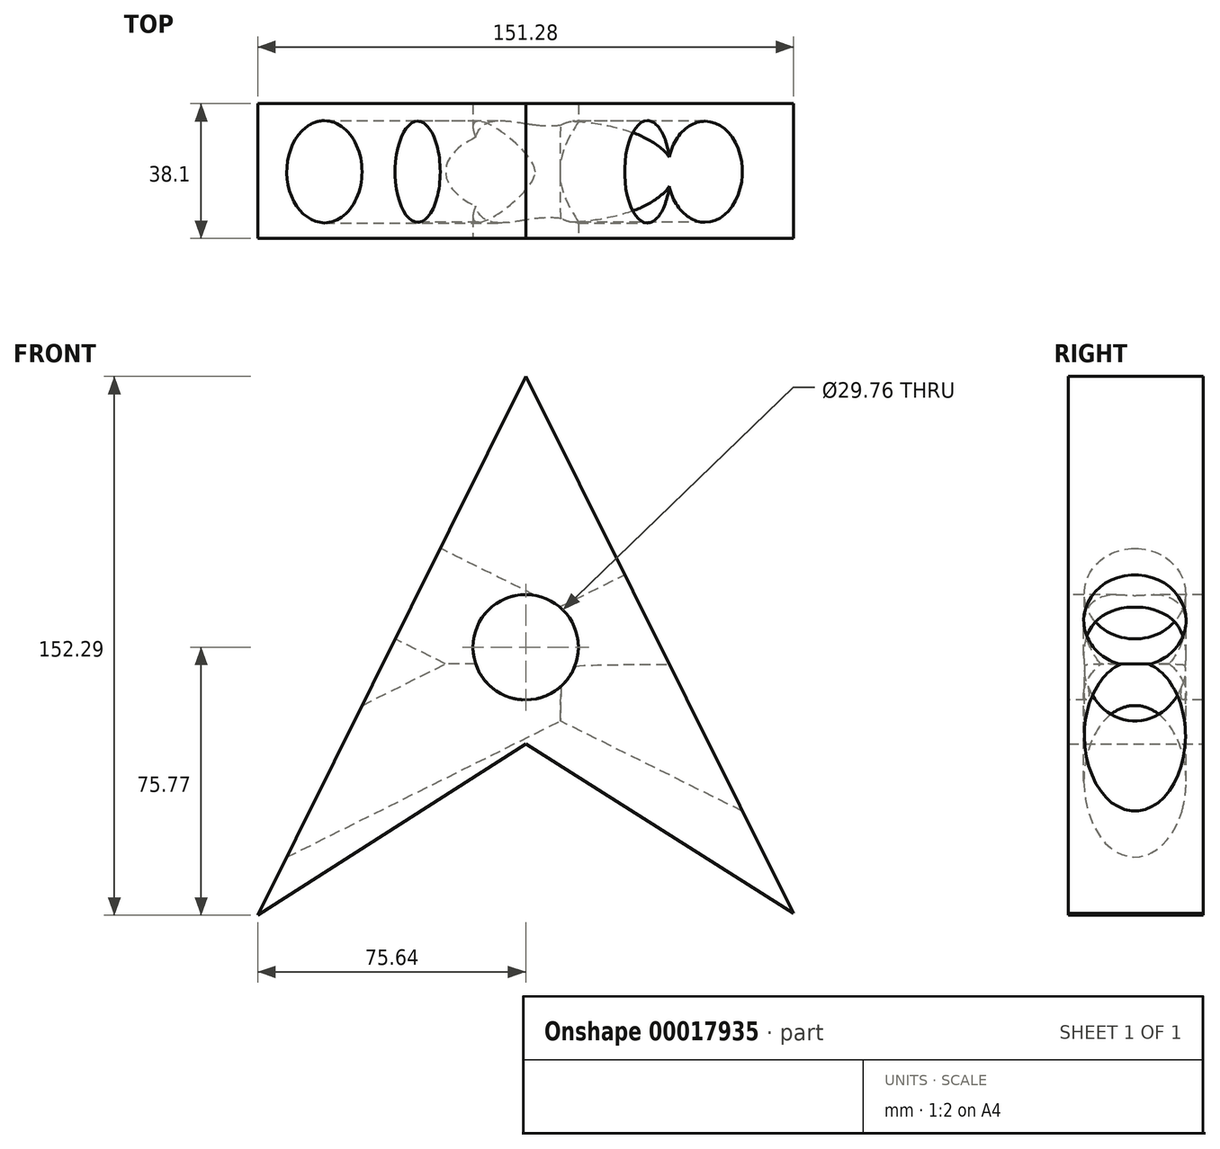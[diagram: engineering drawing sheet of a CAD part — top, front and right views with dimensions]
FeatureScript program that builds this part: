
annotation { "Feature Type Name" : "Feature", "Feature Type Description" : "" }
export const myFeature = defineFeature(function(context is Context, id is Id, definition is map)
    precondition{}
    {
        {
            var Q0;
            Q0=qCreatedBy(makeId("Front.planeOp"),FACE);
            var sketch = newSketch(context, id + "F0", { "sketchPlane" : qUnion([Q0])});
            skLineSegment(sketch, "E0", {"start": v(75.64, -75.27) * mm, "end": v(0, 76.52) * mm});
            skLineSegment(sketch, "E1", {"start": v(0, 76.52) * mm, "end": v(-75.64, -75.77) * mm});
            skLineSegment(sketch, "E2", {"start": v(-75.64, -75.77) * mm, "end": v(0, -27.34) * mm});
            skLineSegment(sketch, "E3", {"start": v(0, -27.34) * mm, "end": v(75.64, -75.27) * mm});
            skSolve(sketch);
        }
        {
            var Q0;
            Q0=makeQuery(id+"F0.imprint","IMPRINT",FACE,{"disambiguationData":[TD([[makeQuery(id+"F0.imprint","IMPRINT",EDGE,{"derivedFrom":sQuery(id+"F0.wireOp",EDGE,"E0")}),1.0]])]});
            extrude(context, id + "F1", {"entities" : qUnion([Q0]), "depth" : 38.1 * mm});
        }
        {
            var Q0;
            Q0=makeQuery(id+"F1.opExtrude","CAP_FACE",FACE,{"disambiguationData":[OSD([sQuery(id+"F0.wireOp",EDGE,"E0"),sQuery(id+"F0.wireOp",EDGE,"E1"),sQuery(id+"F0.wireOp",EDGE,"E2"),sQuery(id+"F0.wireOp",EDGE,"E3")])],"isStart":false});
            var sketch = newSketch(context, id + "F2", { "sketchPlane" : qUnion([Q0])});
            skCircle(sketch, "E4", {"center": v(0, 0) * mm, "radius": 14.88 * mm});
            skSolve(sketch);
        }
        {
            var Q0;
            Q0=makeQuery(id+"F2.imprint","IMPRINT",FACE,{"disambiguationData":[TD([[makeQuery(id+"F2.imprint","IMPRINT",EDGE,{"derivedFrom":sQuery(id+"F2.wireOp",EDGE,"E4")}),1.0]])]});
            extrude(context, id + "F3", {"entities" : qUnion([Q0]), "operationType" : NewBodyOperationType.REMOVE, "endBound" : BoundingType.THROUGH_ALL, "oppositeDirection" : true, "depth" : 25.4 * mm});
        }
        {
            var Q0;
            Q0=makeQuery(id+"F1.opExtrude","SWEPT_FACE",FACE,{"disambiguationData":[OSD([sQuery(id+"F0.wireOp",EDGE,"E0")])]});
            var sketch = newSketch(context, id + "F4", { "sketchPlane" : qUnion([Q0])});
            skCircle(sketch, "E5", {"center": v(-19.26, -8.59) * mm, "radius": 14.44 * mm});
            skSolve(sketch);
        }
        {
            var Q0;
            Q0=makeQuery(id+"F4.imprint","IMPRINT",FACE,{"disambiguationData":[TD([[makeQuery(id+"F4.imprint","IMPRINT",EDGE,{"derivedFrom":sQuery(id+"F4.wireOp",EDGE,"E5")}),1.0]])]});
            extrude(context, id + "F5", {"entities" : qUnion([Q0]), "operationType" : NewBodyOperationType.REMOVE, "endBound" : BoundingType.THROUGH_ALL, "oppositeDirection" : true, "depth" : 38.1 * mm});
        }
        {
            var Q0;
            Q0=makeQuery(id+"F1.opExtrude","SWEPT_FACE",FACE,{"disambiguationData":[OSD([sQuery(id+"F0.wireOp",EDGE,"E1")])]});
            var sketch = newSketch(context, id + "F6", { "sketchPlane" : qUnion([Q0])});
            skCircle(sketch, "E6", {"center": v(19.26, 0) * mm, "radius": 14.3 * mm});
            skSolve(sketch);
        }
        {
            var Q0;
            Q0=makeQuery(id+"F6.imprint","IMPRINT",FACE,{"disambiguationData":[TD([[makeQuery(id+"F6.imprint","IMPRINT",EDGE,{"derivedFrom":sQuery(id+"F6.wireOp",EDGE,"E6")}),1.0]])]});
            extrude(context, id + "F7", {"entities" : qUnion([Q0]), "operationType" : NewBodyOperationType.REMOVE, "endBound" : BoundingType.THROUGH_ALL, "oppositeDirection" : true, "depth" : 25.4 * mm});
        }
    });
